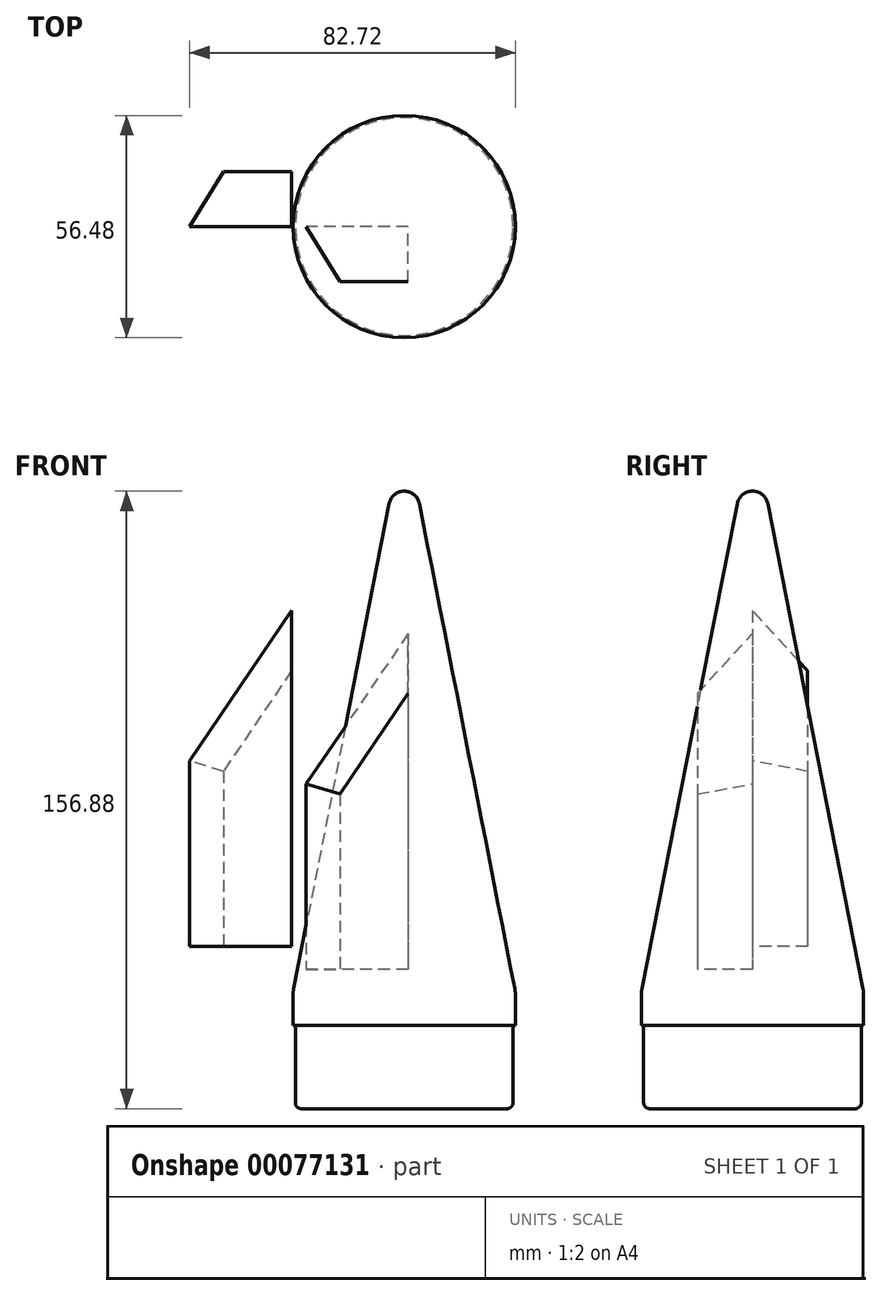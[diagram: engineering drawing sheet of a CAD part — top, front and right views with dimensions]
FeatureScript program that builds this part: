
annotation { "Feature Type Name" : "Feature", "Feature Type Description" : "" }
export const myFeature = defineFeature(function(context is Context, id is Id, definition is map)
    precondition{}
    {
        {
            var Q0;
            Q0=qCreatedBy(makeId("Front.planeOp"),FACE);
            var sketch = newSketch(context, id + "F0", { "sketchPlane" : qUnion([Q0])});
            skLineSegment(sketch, "E0", {"start": v(-33.3, -70.07) * mm, "end": v(-33.3, -70.07) * mm});
            skLineSegment(sketch, "E1", {"start": v(0, -70.07) * mm, "end": v(0, 79.93) * mm});
            skLineSegment(sketch, "E2", {"start": v(0, -70.07) * mm, "end": v(0, -80.07) * mm});
            skLineSegment(sketch, "E3", {"start": v(-32.6, -80.07) * mm, "end": v(-33.3, -80.07) * mm});
            skLineSegment(sketch, "E4", {"start": v(-33.3, -80.07) * mm, "end": v(-33.3, -70.07) * mm});
            skPoint(sketch, "E5.orphan", {"position": v(0, 86.63) * mm});
            skLineSegment(sketch, "E6", {"start": v(-33.3, -70.07) * mm, "end": v(-4.56, 76.18) * mm});
            skLineSegment(sketch, "E7.top", {"start": v(0, -105.07) * mm, "end": v(-32.6, -105.07) * mm});
            skLineSegment(sketch, "E7.left", {"start": v(0, -80.07) * mm, "end": v(0, -105.07) * mm});
            skLineSegment(sketch, "E7.right", {"start": v(-32.6, -80.07) * mm, "end": v(-32.6, -105.07) * mm});
            skArc(sketch, "E8", {"start": v(0, 79.93) * mm, "mid": v(-2.95, 78.87) * mm, "end": v(-4.56, 76.18) * mm});
            skSolve(sketch);
        }
        {
            var Q0;
            {var subQ0=sQuery(id+"F0.wireOp",EDGE,"E2");Q0=makeQuery(id+"F0.imprint","IMPRINT",FACE,{"disambiguationData":[TD([[makeQuery(id+"F0.imprint","IMPRINT",EDGE,{"derivedFrom":subQ0}),-1.0]])]});}
            var Q1;
            Q1=sQuery(id+"F0.wireOp",EDGE,"E1");
            revolve(context, id + "F1", {"entities" : qUnion([Q0]), "axis" : qUnion([Q1]), "revolveType" : RevolveType.FULL});
        }
        {
            var Q0;
            Q0=makeQuery(id+"F1.opRevolve","SWEPT_BODY",BODY,{"disambiguationData":[OSD([sQuery(id+"F0.wireOp",EDGE,"Oh61cgLR-RQo2-T4aV-TcRg-Gp7ijPdUG9jl"),sQuery(id+"F0.wireOp",EDGE,"E1"),sQuery(id+"F0.wireOp",EDGE,"E2"),sQuery(id+"F0.wireOp",EDGE,"E3"),sQuery(id+"F0.wireOp",EDGE,"E4"),sQuery(id+"F0.wireOp",EDGE,"E0"),sQuery(id+"F0.wireOp",EDGE,"dTV1AxgJ-VMAe-DLQO-Zqz3-4UbtDb8FiUJC")])]});
            var Q1;
            Q1=qCreatedBy(makeId("Origin.pointOp"),VERTEX);
            transform(context, id + "F2", {"entities" : qUnion([Q0]), "transformType" : TransformType.SCALE_UNIFORMLY, "scale" : .848, "scalePoint" : qUnion([Q1]), "makeCopy" : false});
        }
        {
            var Q0;
            Q0=qCreatedBy(makeId("Front.planeOp"),FACE);
            var sketch = newSketch(context, id + "F3", { "sketchPlane" : qUnion([Q0])});
            skLineSegment(sketch, "E9", {"start": v(-56.93, -47.9) * mm, "end": v(-56.93, 0) * mm});
            skLineSegment(sketch, "E10", {"start": v(-56.93, 0) * mm, "end": v(-28.6, 41.78) * mm});
            skLineSegment(sketch, "E11", {"start": v(-28.6, 41.78) * mm, "end": v(-28.6, -47.9) * mm});
            skLineSegment(sketch, "E12", {"start": v(-28.6, -47.9) * mm, "end": v(-56.93, -47.9) * mm});
            skSolve(sketch);
        }
        {
            var Q0;
            Q0=makeQuery(id+"F3.imprint","IMPRINT",FACE,{"disambiguationData":[TD([[makeQuery(id+"F3.imprint","IMPRINT",EDGE,{"derivedFrom":sQuery(id+"F3.wireOp",EDGE,"E9")}),-1.0]])]});
            extrude(context, id + "F4", {"entities" : qUnion([Q0]), "depth" : 14 * mm, "offsetDistance" : 25 * mm});
        }
        {
            var Q0;
            Q0=makeQuery(id+"F4.opExtrude","CAP_EDGE",EDGE,{"disambiguationData":[OSD([sQuery(id+"F3.wireOp",EDGE,"E10")])],"isStart":false});
            var Q1;
            Q1=makeQuery(id+"F4.opExtrude","CAP_EDGE",EDGE,{"disambiguationData":[OSD([sQuery(id+"F3.wireOp",EDGE,"E9")])],"isStart":false});
            chamfer(context, id + "F5", {"entities" : qUnion([Q0, Q1]), "chamferType" : ChamferType.TWO_OFFSETS, "width1" : 11 * mm, "oppositeDirection" : false, "width2" : 18 * mm, "tangentPropagation" : true});
        }
        {
            var Q0;
            Q0=makeQuery(id+"F4.opExtrude","SWEPT_BODY",BODY,{"disambiguationData":[OSD([sQuery(id+"F3.wireOp",EDGE,"E9"),sQuery(id+"F3.wireOp",EDGE,"E10"),sQuery(id+"F3.wireOp",EDGE,"E11"),sQuery(id+"F3.wireOp",EDGE,"E12")])]});
            var Q1;
            Q1=qCreatedBy(makeId("Front.planeOp"),FACE);
            mirror(context, id + "F6", {"operationType" : NewBodyOperationType.ADD, "entities" : qUnion([Q0]), "mirrorPlane" : qUnion([Q1])});
        }
        {
            var Q0;
            Q0=makeQuery(id+"F4.opExtrude","SWEPT_BODY",BODY,{"disambiguationData":[OSD([sQuery(id+"F3.wireOp",EDGE,"E9"),sQuery(id+"F3.wireOp",EDGE,"E10"),sQuery(id+"F3.wireOp",EDGE,"E11"),sQuery(id+"F3.wireOp",EDGE,"E12")])]});
            transform(context, id + "F7", {"entities" : qUnion([Q0]), "transformType" : TransformType.TRANSLATION_3D, "dx" : 29.6 * mm, "dy" : 0 * mm, "dz" : -5.8 * mm, "makeCopy" : false});
        }
        {
            var Q0;
            Q0=makeQuery(id+"F1.opRevolve","SWEPT_EDGE",EDGE,{"disambiguationData":[OSD([sQuery(id+"F0.wireOp",EDGE,"E4"),sQuery(id+"F0.wireOp",EDGE,"E6")])]});
            fillet(context, id + "F8", {"entities" : qUnion([Q0]), "radius" : 7.8 * mm, "tangentPropagation" : true, "allowEdgeOverflow" : false});
        }
        {
            var Q0;
            Q0=makeQuery(id+"F1.opRevolve","SWEPT_EDGE",EDGE,{"disambiguationData":[OSD([sQuery(id+"F0.wireOp",EDGE,"E7.top"),sQuery(id+"F0.wireOp",EDGE,"E7.right")])]});
            fillet(context, id + "F9", {"entities" : qUnion([Q0]), "radius" : 1.5 * mm, "tangentPropagation" : true, "allowEdgeOverflow" : false});
        }
        {
            var Q0;
            Q0=qCreatedBy(makeId("Top.planeOp"),FACE);
            cPlane(context, id + "F10", {"entities" : qUnion([Q0]), "cplaneType" : CPlaneType.OFFSET, "offset" : 25 * mm, "oppositeDirection" : true, "width" : 150 * mm, "height" : 150 * mm});
        }
        {
            var Q0;
            Q0=qCreatedBy(makeId("Front.planeOp"),FACE);
            cPlane(context, id + "F12", {"entities" : qUnion([Q0]), "cplaneType" : CPlaneType.OFFSET, "offset" : 35 * mm, "width" : 150 * mm, "height" : 150 * mm});
        }
        {
            var Q0;
            Q0=qCreatedBy(id+"F12.planeOp",FACE);
            var sketch = newSketch(context, id + "F13", { "sketchPlane" : qUnion([Q0])});
            skText(sketch, "E13", { "text": "DC3Dparts", "fontName": "OpenSans-Regular.ttf"});
            const initialGuessF13  = {"E13": [-0.024, -0.07859, 1, 0, 0.007]};
            skSetInitialGuess(sketch, initialGuessF13);
            skSolve(sketch);
        }
        {
            var Q0;
            Q0=qSketchRegion(id+"F13",true);
            var Q1;
            Q1=qCreatedBy(makeId("Front.planeOp"),FACE);
            extrude(context, id + "F14", {"entities" : qUnion([Q0]), "endBound" : BoundingType.UP_TO_SURFACE, "oppositeDirection" : true, "depth" : 25 * mm, "endBoundEntityFace" : qUnion([Q1]), "offsetDistance" : 25 * mm});
        }
        {
            var Q0;
            Q0=qCreatedBy(makeId("Front.planeOp"),FACE);
            var sketch = newSketch(context, id + "F15", { "sketchPlane" : qUnion([Q0])});
            skLineSegment(sketch, "E14.bottom", {"start": v(0, -64.71) * mm, "end": v(-27, -64.71) * mm});
            skLineSegment(sketch, "E14.top", {"start": v(0, -103.72) * mm, "end": v(-27, -103.72) * mm});
            skLineSegment(sketch, "E14.left", {"start": v(0, -64.71) * mm, "end": v(0, -103.72) * mm});
            skLineSegment(sketch, "E14.right", {"start": v(-27, -64.71) * mm, "end": v(-27, -103.72) * mm});
            skSolve(sketch);
        }
        {
            var Q0;
            Q0=makeQuery(id+"F15.imprint","IMPRINT",FACE,{"disambiguationData":[TD([[makeQuery(id+"F15.imprint","IMPRINT",EDGE,{"derivedFrom":sQuery(id+"F15.wireOp",EDGE,"E14.bottom")}),1.0]])]});
            var Q1;
            Q1=sQuery(id+"F15.wireOp",EDGE,"E14.left");
            revolve(context, id + "F16", {"entities" : qUnion([Q0]), "axis" : qUnion([Q1]), "revolveType" : RevolveType.FULL});
        }
        {
            var Q0;
            Q0=makeQuery(id+"F16.opRevolve","SWEPT_BODY",BODY,{"disambiguationData":[OSD([sQuery(id+"F15.wireOp",EDGE,"E14.bottom"),sQuery(id+"F15.wireOp",EDGE,"E14.top"),sQuery(id+"F15.wireOp",EDGE,"E14.left"),sQuery(id+"F15.wireOp",EDGE,"E14.right")])]});
            var Q1;
            Q1=makeQuery(id+"F14.opExtrude","SWEPT_BODY",BODY,{"disambiguationData":[OSD([sQuery(id+"F13.wireOp",EDGE,"E13.sketch_text.stroke-0"),sQuery(id+"F13.wireOp",EDGE,"E13.sketch_text.stroke-1"),sQuery(id+"F13.wireOp",EDGE,"E13.sketch_text.stroke-2"),sQuery(id+"F13.wireOp",EDGE,"E13.sketch_text.stroke-3"),sQuery(id+"F13.wireOp",EDGE,"E13.sketch_text.stroke-4"),sQuery(id+"F13.wireOp",EDGE,"E13.sketch_text.stroke-5"),sQuery(id+"F13.wireOp",EDGE,"E13.sketch_text.stroke-6"),sQuery(id+"F13.wireOp",EDGE,"E13.sketch_text.stroke-7"),sQuery(id+"F13.wireOp",EDGE,"E13.sketch_text.stroke-8"),sQuery(id+"F13.wireOp",EDGE,"E13.sketch_text.stroke-9"),sQuery(id+"F13.wireOp",EDGE,"E13.sketch_text.stroke-10"),sQuery(id+"F13.wireOp",EDGE,"E13.sketch_text.stroke-11"),sQuery(id+"F13.wireOp",EDGE,"E13.sketch_text.stroke-12"),sQuery(id+"F13.wireOp",EDGE,"E13.sketch_text.stroke-13")])]});
            var Q2;
            Q2=makeQuery(id+"F14.opExtrude","SWEPT_BODY",BODY,{"disambiguationData":[OSD([sQuery(id+"F13.wireOp",EDGE,"E13.sketch_text.stroke-14"),sQuery(id+"F13.wireOp",EDGE,"E13.sketch_text.stroke-15"),sQuery(id+"F13.wireOp",EDGE,"E13.sketch_text.stroke-16"),sQuery(id+"F13.wireOp",EDGE,"E13.sketch_text.stroke-17"),sQuery(id+"F13.wireOp",EDGE,"E13.sketch_text.stroke-18"),sQuery(id+"F13.wireOp",EDGE,"E13.sketch_text.stroke-19"),sQuery(id+"F13.wireOp",EDGE,"E13.sketch_text.stroke-20"),sQuery(id+"F13.wireOp",EDGE,"E13.sketch_text.stroke-21"),sQuery(id+"F13.wireOp",EDGE,"E13.sketch_text.stroke-22"),sQuery(id+"F13.wireOp",EDGE,"E13.sketch_text.stroke-23"),sQuery(id+"F13.wireOp",EDGE,"E13.sketch_text.stroke-24"),sQuery(id+"F13.wireOp",EDGE,"E13.sketch_text.stroke-25"),sQuery(id+"F13.wireOp",EDGE,"E13.sketch_text.stroke-26"),sQuery(id+"F13.wireOp",EDGE,"E13.sketch_text.stroke-27"),sQuery(id+"F13.wireOp",EDGE,"E13.sketch_text.stroke-28")])]});
            var Q3;
            Q3=makeQuery(id+"F14.opExtrude","SWEPT_BODY",BODY,{"disambiguationData":[OSD([sQuery(id+"F13.wireOp",EDGE,"E13.sketch_text.stroke-29"),sQuery(id+"F13.wireOp",EDGE,"E13.sketch_text.stroke-30"),sQuery(id+"F13.wireOp",EDGE,"E13.sketch_text.stroke-31"),sQuery(id+"F13.wireOp",EDGE,"E13.sketch_text.stroke-32"),sQuery(id+"F13.wireOp",EDGE,"E13.sketch_text.stroke-33"),sQuery(id+"F13.wireOp",EDGE,"E13.sketch_text.stroke-34"),sQuery(id+"F13.wireOp",EDGE,"E13.sketch_text.stroke-35"),sQuery(id+"F13.wireOp",EDGE,"E13.sketch_text.stroke-36"),sQuery(id+"F13.wireOp",EDGE,"E13.sketch_text.stroke-37"),sQuery(id+"F13.wireOp",EDGE,"E13.sketch_text.stroke-38"),sQuery(id+"F13.wireOp",EDGE,"E13.sketch_text.stroke-39"),sQuery(id+"F13.wireOp",EDGE,"E13.sketch_text.stroke-40"),sQuery(id+"F13.wireOp",EDGE,"E13.sketch_text.stroke-41"),sQuery(id+"F13.wireOp",EDGE,"E13.sketch_text.stroke-42"),sQuery(id+"F13.wireOp",EDGE,"E13.sketch_text.stroke-43"),sQuery(id+"F13.wireOp",EDGE,"E13.sketch_text.stroke-44"),sQuery(id+"F13.wireOp",EDGE,"E13.sketch_text.stroke-45"),sQuery(id+"F13.wireOp",EDGE,"E13.sketch_text.stroke-46"),sQuery(id+"F13.wireOp",EDGE,"E13.sketch_text.stroke-47"),sQuery(id+"F13.wireOp",EDGE,"E13.sketch_text.stroke-48"),sQuery(id+"F13.wireOp",EDGE,"E13.sketch_text.stroke-49"),sQuery(id+"F13.wireOp",EDGE,"E13.sketch_text.stroke-50"),sQuery(id+"F13.wireOp",EDGE,"E13.sketch_text.stroke-51"),sQuery(id+"F13.wireOp",EDGE,"E13.sketch_text.stroke-52"),sQuery(id+"F13.wireOp",EDGE,"E13.sketch_text.stroke-53"),sQuery(id+"F13.wireOp",EDGE,"E13.sketch_text.stroke-54"),sQuery(id+"F13.wireOp",EDGE,"E13.sketch_text.stroke-55"),sQuery(id+"F13.wireOp",EDGE,"E13.sketch_text.stroke-56")])]});
            var Q4;
            Q4=makeQuery(id+"F14.opExtrude","SWEPT_BODY",BODY,{"disambiguationData":[OSD([sQuery(id+"F13.wireOp",EDGE,"E13.sketch_text.stroke-57"),sQuery(id+"F13.wireOp",EDGE,"E13.sketch_text.stroke-58"),sQuery(id+"F13.wireOp",EDGE,"E13.sketch_text.stroke-59"),sQuery(id+"F13.wireOp",EDGE,"E13.sketch_text.stroke-60"),sQuery(id+"F13.wireOp",EDGE,"E13.sketch_text.stroke-61"),sQuery(id+"F13.wireOp",EDGE,"E13.sketch_text.stroke-62"),sQuery(id+"F13.wireOp",EDGE,"E13.sketch_text.stroke-63"),sQuery(id+"F13.wireOp",EDGE,"E13.sketch_text.stroke-64"),sQuery(id+"F13.wireOp",EDGE,"E13.sketch_text.stroke-65"),sQuery(id+"F13.wireOp",EDGE,"E13.sketch_text.stroke-66"),sQuery(id+"F13.wireOp",EDGE,"E13.sketch_text.stroke-67"),sQuery(id+"F13.wireOp",EDGE,"E13.sketch_text.stroke-68"),sQuery(id+"F13.wireOp",EDGE,"E13.sketch_text.stroke-69"),sQuery(id+"F13.wireOp",EDGE,"E13.sketch_text.stroke-70")])]});
            var Q5;
            Q5=makeQuery(id+"F14.opExtrude","SWEPT_BODY",BODY,{"disambiguationData":[OSD([sQuery(id+"F13.wireOp",EDGE,"E13.sketch_text.stroke-71"),sQuery(id+"F13.wireOp",EDGE,"E13.sketch_text.stroke-72"),sQuery(id+"F13.wireOp",EDGE,"E13.sketch_text.stroke-73"),sQuery(id+"F13.wireOp",EDGE,"E13.sketch_text.stroke-74"),sQuery(id+"F13.wireOp",EDGE,"E13.sketch_text.stroke-75"),sQuery(id+"F13.wireOp",EDGE,"E13.sketch_text.stroke-76"),sQuery(id+"F13.wireOp",EDGE,"E13.sketch_text.stroke-77"),sQuery(id+"F13.wireOp",EDGE,"E13.sketch_text.stroke-78"),sQuery(id+"F13.wireOp",EDGE,"E13.sketch_text.stroke-79"),sQuery(id+"F13.wireOp",EDGE,"E13.sketch_text.stroke-80"),sQuery(id+"F13.wireOp",EDGE,"E13.sketch_text.stroke-81"),sQuery(id+"F13.wireOp",EDGE,"E13.sketch_text.stroke-82"),sQuery(id+"F13.wireOp",EDGE,"E13.sketch_text.stroke-83"),sQuery(id+"F13.wireOp",EDGE,"E13.sketch_text.stroke-84"),sQuery(id+"F13.wireOp",EDGE,"E13.sketch_text.stroke-85"),sQuery(id+"F13.wireOp",EDGE,"E13.sketch_text.stroke-86"),sQuery(id+"F13.wireOp",EDGE,"E13.sketch_text.stroke-87"),sQuery(id+"F13.wireOp",EDGE,"E13.sketch_text.stroke-88"),sQuery(id+"F13.wireOp",EDGE,"E13.sketch_text.stroke-89"),sQuery(id+"F13.wireOp",EDGE,"E13.sketch_text.stroke-90"),sQuery(id+"F13.wireOp",EDGE,"E13.sketch_text.stroke-91"),sQuery(id+"F13.wireOp",EDGE,"E13.sketch_text.stroke-92"),sQuery(id+"F13.wireOp",EDGE,"E13.sketch_text.stroke-93"),sQuery(id+"F13.wireOp",EDGE,"E13.sketch_text.stroke-94"),sQuery(id+"F13.wireOp",EDGE,"E13.sketch_text.stroke-95")])]});
            var Q6;
            Q6=makeQuery(id+"F14.opExtrude","SWEPT_BODY",BODY,{"disambiguationData":[OSD([sQuery(id+"F13.wireOp",EDGE,"E13.sketch_text.stroke-96"),sQuery(id+"F13.wireOp",EDGE,"E13.sketch_text.stroke-97"),sQuery(id+"F13.wireOp",EDGE,"E13.sketch_text.stroke-98"),sQuery(id+"F13.wireOp",EDGE,"E13.sketch_text.stroke-99"),sQuery(id+"F13.wireOp",EDGE,"E13.sketch_text.stroke-100"),sQuery(id+"F13.wireOp",EDGE,"E13.sketch_text.stroke-101"),sQuery(id+"F13.wireOp",EDGE,"E13.sketch_text.stroke-102"),sQuery(id+"F13.wireOp",EDGE,"E13.sketch_text.stroke-103"),sQuery(id+"F13.wireOp",EDGE,"E13.sketch_text.stroke-104"),sQuery(id+"F13.wireOp",EDGE,"E13.sketch_text.stroke-105"),sQuery(id+"F13.wireOp",EDGE,"E13.sketch_text.stroke-106"),sQuery(id+"F13.wireOp",EDGE,"E13.sketch_text.stroke-107"),sQuery(id+"F13.wireOp",EDGE,"E13.sketch_text.stroke-108"),sQuery(id+"F13.wireOp",EDGE,"E13.sketch_text.stroke-109"),sQuery(id+"F13.wireOp",EDGE,"E13.sketch_text.stroke-110"),sQuery(id+"F13.wireOp",EDGE,"E13.sketch_text.stroke-111"),sQuery(id+"F13.wireOp",EDGE,"E13.sketch_text.stroke-112"),sQuery(id+"F13.wireOp",EDGE,"E13.sketch_text.stroke-113"),sQuery(id+"F13.wireOp",EDGE,"E13.sketch_text.stroke-114"),sQuery(id+"F13.wireOp",EDGE,"E13.sketch_text.stroke-115"),sQuery(id+"F13.wireOp",EDGE,"E13.sketch_text.stroke-116"),sQuery(id+"F13.wireOp",EDGE,"E13.sketch_text.stroke-117"),sQuery(id+"F13.wireOp",EDGE,"E13.sketch_text.stroke-118"),sQuery(id+"F13.wireOp",EDGE,"E13.sketch_text.stroke-119"),sQuery(id+"F13.wireOp",EDGE,"E13.sketch_text.stroke-120"),sQuery(id+"F13.wireOp",EDGE,"E13.sketch_text.stroke-121"),sQuery(id+"F13.wireOp",EDGE,"E13.sketch_text.stroke-122")])]});
            var Q7;
            Q7=makeQuery(id+"F14.opExtrude","SWEPT_BODY",BODY,{"disambiguationData":[OSD([sQuery(id+"F13.wireOp",EDGE,"E13.sketch_text.stroke-123"),sQuery(id+"F13.wireOp",EDGE,"E13.sketch_text.stroke-124"),sQuery(id+"F13.wireOp",EDGE,"E13.sketch_text.stroke-125"),sQuery(id+"F13.wireOp",EDGE,"E13.sketch_text.stroke-126"),sQuery(id+"F13.wireOp",EDGE,"E13.sketch_text.stroke-127"),sQuery(id+"F13.wireOp",EDGE,"E13.sketch_text.stroke-128"),sQuery(id+"F13.wireOp",EDGE,"E13.sketch_text.stroke-129"),sQuery(id+"F13.wireOp",EDGE,"E13.sketch_text.stroke-130"),sQuery(id+"F13.wireOp",EDGE,"E13.sketch_text.stroke-131"),sQuery(id+"F13.wireOp",EDGE,"E13.sketch_text.stroke-132"),sQuery(id+"F13.wireOp",EDGE,"E13.sketch_text.stroke-133"),sQuery(id+"F13.wireOp",EDGE,"E13.sketch_text.stroke-134"),sQuery(id+"F13.wireOp",EDGE,"E13.sketch_text.stroke-135")])]});
            var Q8;
            Q8=makeQuery(id+"F14.opExtrude","SWEPT_BODY",BODY,{"disambiguationData":[OSD([sQuery(id+"F13.wireOp",EDGE,"E13.sketch_text.stroke-136"),sQuery(id+"F13.wireOp",EDGE,"E13.sketch_text.stroke-137"),sQuery(id+"F13.wireOp",EDGE,"E13.sketch_text.stroke-138"),sQuery(id+"F13.wireOp",EDGE,"E13.sketch_text.stroke-139"),sQuery(id+"F13.wireOp",EDGE,"E13.sketch_text.stroke-140"),sQuery(id+"F13.wireOp",EDGE,"E13.sketch_text.stroke-141"),sQuery(id+"F13.wireOp",EDGE,"E13.sketch_text.stroke-142"),sQuery(id+"F13.wireOp",EDGE,"E13.sketch_text.stroke-143"),sQuery(id+"F13.wireOp",EDGE,"E13.sketch_text.stroke-144"),sQuery(id+"F13.wireOp",EDGE,"E13.sketch_text.stroke-145"),sQuery(id+"F13.wireOp",EDGE,"E13.sketch_text.stroke-146"),sQuery(id+"F13.wireOp",EDGE,"E13.sketch_text.stroke-147"),sQuery(id+"F13.wireOp",EDGE,"E13.sketch_text.stroke-148"),sQuery(id+"F13.wireOp",EDGE,"E13.sketch_text.stroke-149"),sQuery(id+"F13.wireOp",EDGE,"E13.sketch_text.stroke-150"),sQuery(id+"F13.wireOp",EDGE,"E13.sketch_text.stroke-151"),sQuery(id+"F13.wireOp",EDGE,"E13.sketch_text.stroke-152"),sQuery(id+"F13.wireOp",EDGE,"E13.sketch_text.stroke-153"),sQuery(id+"F13.wireOp",EDGE,"E13.sketch_text.stroke-154")])]});
            var Q9;
            Q9=makeQuery(id+"F14.opExtrude","SWEPT_BODY",BODY,{"disambiguationData":[OSD([sQuery(id+"F13.wireOp",EDGE,"E13.sketch_text.stroke-155"),sQuery(id+"F13.wireOp",EDGE,"E13.sketch_text.stroke-156"),sQuery(id+"F13.wireOp",EDGE,"E13.sketch_text.stroke-157"),sQuery(id+"F13.wireOp",EDGE,"E13.sketch_text.stroke-158"),sQuery(id+"F13.wireOp",EDGE,"E13.sketch_text.stroke-159"),sQuery(id+"F13.wireOp",EDGE,"E13.sketch_text.stroke-160"),sQuery(id+"F13.wireOp",EDGE,"E13.sketch_text.stroke-161"),sQuery(id+"F13.wireOp",EDGE,"E13.sketch_text.stroke-162"),sQuery(id+"F13.wireOp",EDGE,"E13.sketch_text.stroke-163"),sQuery(id+"F13.wireOp",EDGE,"E13.sketch_text.stroke-164"),sQuery(id+"F13.wireOp",EDGE,"E13.sketch_text.stroke-165"),sQuery(id+"F13.wireOp",EDGE,"E13.sketch_text.stroke-166"),sQuery(id+"F13.wireOp",EDGE,"E13.sketch_text.stroke-167"),sQuery(id+"F13.wireOp",EDGE,"E13.sketch_text.stroke-168"),sQuery(id+"F13.wireOp",EDGE,"E13.sketch_text.stroke-169"),sQuery(id+"F13.wireOp",EDGE,"E13.sketch_text.stroke-170"),sQuery(id+"F13.wireOp",EDGE,"E13.sketch_text.stroke-171"),sQuery(id+"F13.wireOp",EDGE,"E13.sketch_text.stroke-172"),sQuery(id+"F13.wireOp",EDGE,"E13.sketch_text.stroke-173"),sQuery(id+"F13.wireOp",EDGE,"E13.sketch_text.stroke-174"),sQuery(id+"F13.wireOp",EDGE,"E13.sketch_text.stroke-175"),sQuery(id+"F13.wireOp",EDGE,"E13.sketch_text.stroke-176"),sQuery(id+"F13.wireOp",EDGE,"E13.sketch_text.stroke-177"),sQuery(id+"F13.wireOp",EDGE,"E13.sketch_text.stroke-178"),sQuery(id+"F13.wireOp",EDGE,"E13.sketch_text.stroke-179")])]});
            booleanBodies(context, id + "F17", {"operationType" : BooleanOperationType.SUBTRACTION, "tools" : qUnion([Q0]), "targets" : qUnion([Q1, Q2, Q3, Q4, Q5, Q6, Q7, Q8, Q9])});
        }
        {
            var Q0;
            Q0=makeQuery(id+"F14.opExtrude","SWEPT_BODY",BODY,{"disambiguationData":[OSD([sQuery(id+"F13.wireOp",EDGE,"E13.sketch_text.stroke-0"),sQuery(id+"F13.wireOp",EDGE,"E13.sketch_text.stroke-1"),sQuery(id+"F13.wireOp",EDGE,"E13.sketch_text.stroke-2"),sQuery(id+"F13.wireOp",EDGE,"E13.sketch_text.stroke-3"),sQuery(id+"F13.wireOp",EDGE,"E13.sketch_text.stroke-4"),sQuery(id+"F13.wireOp",EDGE,"E13.sketch_text.stroke-5"),sQuery(id+"F13.wireOp",EDGE,"E13.sketch_text.stroke-6"),sQuery(id+"F13.wireOp",EDGE,"E13.sketch_text.stroke-7"),sQuery(id+"F13.wireOp",EDGE,"E13.sketch_text.stroke-8"),sQuery(id+"F13.wireOp",EDGE,"E13.sketch_text.stroke-9"),sQuery(id+"F13.wireOp",EDGE,"E13.sketch_text.stroke-10"),sQuery(id+"F13.wireOp",EDGE,"E13.sketch_text.stroke-11"),sQuery(id+"F13.wireOp",EDGE,"E13.sketch_text.stroke-12"),sQuery(id+"F13.wireOp",EDGE,"E13.sketch_text.stroke-13")])]});
            var Q1;
            Q1=makeQuery(id+"F14.opExtrude","SWEPT_BODY",BODY,{"disambiguationData":[OSD([sQuery(id+"F13.wireOp",EDGE,"E13.sketch_text.stroke-14"),sQuery(id+"F13.wireOp",EDGE,"E13.sketch_text.stroke-15"),sQuery(id+"F13.wireOp",EDGE,"E13.sketch_text.stroke-16"),sQuery(id+"F13.wireOp",EDGE,"E13.sketch_text.stroke-17"),sQuery(id+"F13.wireOp",EDGE,"E13.sketch_text.stroke-18"),sQuery(id+"F13.wireOp",EDGE,"E13.sketch_text.stroke-19"),sQuery(id+"F13.wireOp",EDGE,"E13.sketch_text.stroke-20"),sQuery(id+"F13.wireOp",EDGE,"E13.sketch_text.stroke-21"),sQuery(id+"F13.wireOp",EDGE,"E13.sketch_text.stroke-22"),sQuery(id+"F13.wireOp",EDGE,"E13.sketch_text.stroke-23"),sQuery(id+"F13.wireOp",EDGE,"E13.sketch_text.stroke-24"),sQuery(id+"F13.wireOp",EDGE,"E13.sketch_text.stroke-25"),sQuery(id+"F13.wireOp",EDGE,"E13.sketch_text.stroke-26"),sQuery(id+"F13.wireOp",EDGE,"E13.sketch_text.stroke-27"),sQuery(id+"F13.wireOp",EDGE,"E13.sketch_text.stroke-28")])]});
            var Q2;
            Q2=makeQuery(id+"F14.opExtrude","SWEPT_BODY",BODY,{"disambiguationData":[OSD([sQuery(id+"F13.wireOp",EDGE,"E13.sketch_text.stroke-29"),sQuery(id+"F13.wireOp",EDGE,"E13.sketch_text.stroke-30"),sQuery(id+"F13.wireOp",EDGE,"E13.sketch_text.stroke-31"),sQuery(id+"F13.wireOp",EDGE,"E13.sketch_text.stroke-32"),sQuery(id+"F13.wireOp",EDGE,"E13.sketch_text.stroke-33"),sQuery(id+"F13.wireOp",EDGE,"E13.sketch_text.stroke-34"),sQuery(id+"F13.wireOp",EDGE,"E13.sketch_text.stroke-35"),sQuery(id+"F13.wireOp",EDGE,"E13.sketch_text.stroke-36"),sQuery(id+"F13.wireOp",EDGE,"E13.sketch_text.stroke-37"),sQuery(id+"F13.wireOp",EDGE,"E13.sketch_text.stroke-38"),sQuery(id+"F13.wireOp",EDGE,"E13.sketch_text.stroke-39"),sQuery(id+"F13.wireOp",EDGE,"E13.sketch_text.stroke-40"),sQuery(id+"F13.wireOp",EDGE,"E13.sketch_text.stroke-41"),sQuery(id+"F13.wireOp",EDGE,"E13.sketch_text.stroke-42"),sQuery(id+"F13.wireOp",EDGE,"E13.sketch_text.stroke-43"),sQuery(id+"F13.wireOp",EDGE,"E13.sketch_text.stroke-44"),sQuery(id+"F13.wireOp",EDGE,"E13.sketch_text.stroke-45"),sQuery(id+"F13.wireOp",EDGE,"E13.sketch_text.stroke-46"),sQuery(id+"F13.wireOp",EDGE,"E13.sketch_text.stroke-47"),sQuery(id+"F13.wireOp",EDGE,"E13.sketch_text.stroke-48"),sQuery(id+"F13.wireOp",EDGE,"E13.sketch_text.stroke-49"),sQuery(id+"F13.wireOp",EDGE,"E13.sketch_text.stroke-50"),sQuery(id+"F13.wireOp",EDGE,"E13.sketch_text.stroke-51"),sQuery(id+"F13.wireOp",EDGE,"E13.sketch_text.stroke-52"),sQuery(id+"F13.wireOp",EDGE,"E13.sketch_text.stroke-53"),sQuery(id+"F13.wireOp",EDGE,"E13.sketch_text.stroke-54"),sQuery(id+"F13.wireOp",EDGE,"E13.sketch_text.stroke-55"),sQuery(id+"F13.wireOp",EDGE,"E13.sketch_text.stroke-56")])]});
            var Q3;
            Q3=makeQuery(id+"F14.opExtrude","SWEPT_BODY",BODY,{"disambiguationData":[OSD([sQuery(id+"F13.wireOp",EDGE,"E13.sketch_text.stroke-57"),sQuery(id+"F13.wireOp",EDGE,"E13.sketch_text.stroke-58"),sQuery(id+"F13.wireOp",EDGE,"E13.sketch_text.stroke-59"),sQuery(id+"F13.wireOp",EDGE,"E13.sketch_text.stroke-60"),sQuery(id+"F13.wireOp",EDGE,"E13.sketch_text.stroke-61"),sQuery(id+"F13.wireOp",EDGE,"E13.sketch_text.stroke-62"),sQuery(id+"F13.wireOp",EDGE,"E13.sketch_text.stroke-63"),sQuery(id+"F13.wireOp",EDGE,"E13.sketch_text.stroke-64"),sQuery(id+"F13.wireOp",EDGE,"E13.sketch_text.stroke-65"),sQuery(id+"F13.wireOp",EDGE,"E13.sketch_text.stroke-66"),sQuery(id+"F13.wireOp",EDGE,"E13.sketch_text.stroke-67"),sQuery(id+"F13.wireOp",EDGE,"E13.sketch_text.stroke-68"),sQuery(id+"F13.wireOp",EDGE,"E13.sketch_text.stroke-69"),sQuery(id+"F13.wireOp",EDGE,"E13.sketch_text.stroke-70")])]});
            var Q4;
            Q4=makeQuery(id+"F14.opExtrude","SWEPT_BODY",BODY,{"disambiguationData":[OSD([sQuery(id+"F13.wireOp",EDGE,"E13.sketch_text.stroke-71"),sQuery(id+"F13.wireOp",EDGE,"E13.sketch_text.stroke-72"),sQuery(id+"F13.wireOp",EDGE,"E13.sketch_text.stroke-73"),sQuery(id+"F13.wireOp",EDGE,"E13.sketch_text.stroke-74"),sQuery(id+"F13.wireOp",EDGE,"E13.sketch_text.stroke-75"),sQuery(id+"F13.wireOp",EDGE,"E13.sketch_text.stroke-76"),sQuery(id+"F13.wireOp",EDGE,"E13.sketch_text.stroke-77"),sQuery(id+"F13.wireOp",EDGE,"E13.sketch_text.stroke-78"),sQuery(id+"F13.wireOp",EDGE,"E13.sketch_text.stroke-79"),sQuery(id+"F13.wireOp",EDGE,"E13.sketch_text.stroke-80"),sQuery(id+"F13.wireOp",EDGE,"E13.sketch_text.stroke-81"),sQuery(id+"F13.wireOp",EDGE,"E13.sketch_text.stroke-82"),sQuery(id+"F13.wireOp",EDGE,"E13.sketch_text.stroke-83"),sQuery(id+"F13.wireOp",EDGE,"E13.sketch_text.stroke-84"),sQuery(id+"F13.wireOp",EDGE,"E13.sketch_text.stroke-85"),sQuery(id+"F13.wireOp",EDGE,"E13.sketch_text.stroke-86"),sQuery(id+"F13.wireOp",EDGE,"E13.sketch_text.stroke-87"),sQuery(id+"F13.wireOp",EDGE,"E13.sketch_text.stroke-88"),sQuery(id+"F13.wireOp",EDGE,"E13.sketch_text.stroke-89"),sQuery(id+"F13.wireOp",EDGE,"E13.sketch_text.stroke-90"),sQuery(id+"F13.wireOp",EDGE,"E13.sketch_text.stroke-91"),sQuery(id+"F13.wireOp",EDGE,"E13.sketch_text.stroke-92"),sQuery(id+"F13.wireOp",EDGE,"E13.sketch_text.stroke-93"),sQuery(id+"F13.wireOp",EDGE,"E13.sketch_text.stroke-94"),sQuery(id+"F13.wireOp",EDGE,"E13.sketch_text.stroke-95")])]});
            var Q5;
            Q5=makeQuery(id+"F14.opExtrude","SWEPT_BODY",BODY,{"disambiguationData":[OSD([sQuery(id+"F13.wireOp",EDGE,"E13.sketch_text.stroke-96"),sQuery(id+"F13.wireOp",EDGE,"E13.sketch_text.stroke-97"),sQuery(id+"F13.wireOp",EDGE,"E13.sketch_text.stroke-98"),sQuery(id+"F13.wireOp",EDGE,"E13.sketch_text.stroke-99"),sQuery(id+"F13.wireOp",EDGE,"E13.sketch_text.stroke-100"),sQuery(id+"F13.wireOp",EDGE,"E13.sketch_text.stroke-101"),sQuery(id+"F13.wireOp",EDGE,"E13.sketch_text.stroke-102"),sQuery(id+"F13.wireOp",EDGE,"E13.sketch_text.stroke-103"),sQuery(id+"F13.wireOp",EDGE,"E13.sketch_text.stroke-104"),sQuery(id+"F13.wireOp",EDGE,"E13.sketch_text.stroke-105"),sQuery(id+"F13.wireOp",EDGE,"E13.sketch_text.stroke-106"),sQuery(id+"F13.wireOp",EDGE,"E13.sketch_text.stroke-107"),sQuery(id+"F13.wireOp",EDGE,"E13.sketch_text.stroke-108"),sQuery(id+"F13.wireOp",EDGE,"E13.sketch_text.stroke-109"),sQuery(id+"F13.wireOp",EDGE,"E13.sketch_text.stroke-110"),sQuery(id+"F13.wireOp",EDGE,"E13.sketch_text.stroke-111"),sQuery(id+"F13.wireOp",EDGE,"E13.sketch_text.stroke-112"),sQuery(id+"F13.wireOp",EDGE,"E13.sketch_text.stroke-113"),sQuery(id+"F13.wireOp",EDGE,"E13.sketch_text.stroke-114"),sQuery(id+"F13.wireOp",EDGE,"E13.sketch_text.stroke-115"),sQuery(id+"F13.wireOp",EDGE,"E13.sketch_text.stroke-116"),sQuery(id+"F13.wireOp",EDGE,"E13.sketch_text.stroke-117"),sQuery(id+"F13.wireOp",EDGE,"E13.sketch_text.stroke-118"),sQuery(id+"F13.wireOp",EDGE,"E13.sketch_text.stroke-119"),sQuery(id+"F13.wireOp",EDGE,"E13.sketch_text.stroke-120"),sQuery(id+"F13.wireOp",EDGE,"E13.sketch_text.stroke-121"),sQuery(id+"F13.wireOp",EDGE,"E13.sketch_text.stroke-122")])]});
            var Q6;
            Q6=makeQuery(id+"F14.opExtrude","SWEPT_BODY",BODY,{"disambiguationData":[OSD([sQuery(id+"F13.wireOp",EDGE,"E13.sketch_text.stroke-123"),sQuery(id+"F13.wireOp",EDGE,"E13.sketch_text.stroke-124"),sQuery(id+"F13.wireOp",EDGE,"E13.sketch_text.stroke-125"),sQuery(id+"F13.wireOp",EDGE,"E13.sketch_text.stroke-126"),sQuery(id+"F13.wireOp",EDGE,"E13.sketch_text.stroke-127"),sQuery(id+"F13.wireOp",EDGE,"E13.sketch_text.stroke-128"),sQuery(id+"F13.wireOp",EDGE,"E13.sketch_text.stroke-129"),sQuery(id+"F13.wireOp",EDGE,"E13.sketch_text.stroke-130"),sQuery(id+"F13.wireOp",EDGE,"E13.sketch_text.stroke-131"),sQuery(id+"F13.wireOp",EDGE,"E13.sketch_text.stroke-132"),sQuery(id+"F13.wireOp",EDGE,"E13.sketch_text.stroke-133"),sQuery(id+"F13.wireOp",EDGE,"E13.sketch_text.stroke-134"),sQuery(id+"F13.wireOp",EDGE,"E13.sketch_text.stroke-135")])]});
            var Q7;
            Q7=makeQuery(id+"F14.opExtrude","SWEPT_BODY",BODY,{"disambiguationData":[OSD([sQuery(id+"F13.wireOp",EDGE,"E13.sketch_text.stroke-136"),sQuery(id+"F13.wireOp",EDGE,"E13.sketch_text.stroke-137"),sQuery(id+"F13.wireOp",EDGE,"E13.sketch_text.stroke-138"),sQuery(id+"F13.wireOp",EDGE,"E13.sketch_text.stroke-139"),sQuery(id+"F13.wireOp",EDGE,"E13.sketch_text.stroke-140"),sQuery(id+"F13.wireOp",EDGE,"E13.sketch_text.stroke-141"),sQuery(id+"F13.wireOp",EDGE,"E13.sketch_text.stroke-142"),sQuery(id+"F13.wireOp",EDGE,"E13.sketch_text.stroke-143"),sQuery(id+"F13.wireOp",EDGE,"E13.sketch_text.stroke-144"),sQuery(id+"F13.wireOp",EDGE,"E13.sketch_text.stroke-145"),sQuery(id+"F13.wireOp",EDGE,"E13.sketch_text.stroke-146"),sQuery(id+"F13.wireOp",EDGE,"E13.sketch_text.stroke-147"),sQuery(id+"F13.wireOp",EDGE,"E13.sketch_text.stroke-148"),sQuery(id+"F13.wireOp",EDGE,"E13.sketch_text.stroke-149"),sQuery(id+"F13.wireOp",EDGE,"E13.sketch_text.stroke-150"),sQuery(id+"F13.wireOp",EDGE,"E13.sketch_text.stroke-151"),sQuery(id+"F13.wireOp",EDGE,"E13.sketch_text.stroke-152"),sQuery(id+"F13.wireOp",EDGE,"E13.sketch_text.stroke-153"),sQuery(id+"F13.wireOp",EDGE,"E13.sketch_text.stroke-154")])]});
            var Q8;
            Q8=makeQuery(id+"F14.opExtrude","SWEPT_BODY",BODY,{"disambiguationData":[OSD([sQuery(id+"F13.wireOp",EDGE,"E13.sketch_text.stroke-155"),sQuery(id+"F13.wireOp",EDGE,"E13.sketch_text.stroke-156"),sQuery(id+"F13.wireOp",EDGE,"E13.sketch_text.stroke-157"),sQuery(id+"F13.wireOp",EDGE,"E13.sketch_text.stroke-158"),sQuery(id+"F13.wireOp",EDGE,"E13.sketch_text.stroke-159"),sQuery(id+"F13.wireOp",EDGE,"E13.sketch_text.stroke-160"),sQuery(id+"F13.wireOp",EDGE,"E13.sketch_text.stroke-161"),sQuery(id+"F13.wireOp",EDGE,"E13.sketch_text.stroke-162"),sQuery(id+"F13.wireOp",EDGE,"E13.sketch_text.stroke-163"),sQuery(id+"F13.wireOp",EDGE,"E13.sketch_text.stroke-164"),sQuery(id+"F13.wireOp",EDGE,"E13.sketch_text.stroke-165"),sQuery(id+"F13.wireOp",EDGE,"E13.sketch_text.stroke-166"),sQuery(id+"F13.wireOp",EDGE,"E13.sketch_text.stroke-167"),sQuery(id+"F13.wireOp",EDGE,"E13.sketch_text.stroke-168"),sQuery(id+"F13.wireOp",EDGE,"E13.sketch_text.stroke-169"),sQuery(id+"F13.wireOp",EDGE,"E13.sketch_text.stroke-170"),sQuery(id+"F13.wireOp",EDGE,"E13.sketch_text.stroke-171"),sQuery(id+"F13.wireOp",EDGE,"E13.sketch_text.stroke-172"),sQuery(id+"F13.wireOp",EDGE,"E13.sketch_text.stroke-173"),sQuery(id+"F13.wireOp",EDGE,"E13.sketch_text.stroke-174"),sQuery(id+"F13.wireOp",EDGE,"E13.sketch_text.stroke-175"),sQuery(id+"F13.wireOp",EDGE,"E13.sketch_text.stroke-176"),sQuery(id+"F13.wireOp",EDGE,"E13.sketch_text.stroke-177"),sQuery(id+"F13.wireOp",EDGE,"E13.sketch_text.stroke-178"),sQuery(id+"F13.wireOp",EDGE,"E13.sketch_text.stroke-179")])]});
            var Q9;
            Q9=makeQuery(id+"F4.opExtrude","SWEPT_BODY",BODY,{"disambiguationData":[OSD([sQuery(id+"F3.wireOp",EDGE,"E9"),sQuery(id+"F3.wireOp",EDGE,"E10"),sQuery(id+"F3.wireOp",EDGE,"E11"),sQuery(id+"F3.wireOp",EDGE,"E12")])]});
            booleanBodies(context, id + "F18", {"operationType" : BooleanOperationType.SUBTRACTION, "tools" : qUnion([Q0, Q1, Q2, Q3, Q4, Q5, Q6, Q7, Q8]), "targets" : qUnion([Q9])});
        }
        {
            var Q0;
            Q0=qCreatedBy(id+"F10.planeOp",FACE);
            var sketch = newSketch(context, id + "F19", { "sketchPlane" : qUnion([Q0])});
            skCircle(sketch, "E15", {"center": v(0, 21.08) * mm, "radius": 2 * mm});
            skSolve(sketch);
        }
        {
            var Q0;
            Q0=makeQuery(id+"F19.imprint","IMPRINT",FACE,{"disambiguationData":[TD([[makeQuery(id+"F19.imprint","IMPRINT",EDGE,{"derivedFrom":sQuery(id+"F19.wireOp",EDGE,"E15")}),1.0]])]});
            extrude(context, id + "F20", {"entities" : qUnion([Q0]), "depth" : 25 * mm, "offsetDistance" : 25 * mm});
        }
        {
            var Q0;
            Q0=makeQuery(id+"F20.opExtrude","CAP_EDGE",EDGE,{"disambiguationData":[OSD([sQuery(id+"F19.wireOp",EDGE,"E15")])],"isStart":true});
            fillet(context, id + "F21", {"entities" : qUnion([Q0]), "radius" : 2 * mm, "tangentPropagation" : true, "allowEdgeOverflow" : false});
        }
        {
            var Q0;
            Q0=makeQuery(id+"F20.opExtrude","SWEPT_BODY",BODY,{"disambiguationData":[OSD([sQuery(id+"F19.wireOp",EDGE,"E15")])]});
            transform(context, id + "F22", {"entities" : qUnion([Q0]), "transformType" : TransformType.TRANSLATION_3D, "dx" : 16.4 * mm, "dy" : -4.8 * mm, "dz" : -10.6 * mm, "makeCopy" : true});
        }
        {
            var Q0;
            Q0=makeQuery(id+"F20.opExtrude","SWEPT_BODY",BODY,{"disambiguationData":[OSD([sQuery(id+"F19.wireOp",EDGE,"E15")])]});
            transform(context, id + "F23", {"entities" : qUnion([Q0]), "transformType" : TransformType.TRANSLATION_3D, "dx" : 8.3 * mm, "dy" : -2.5 * mm, "dz" : 0 * mm, "makeCopy" : false});
        }
        {
            var Q0;
            Q0=makeQuery(id+"F20.opExtrude","SWEPT_BODY",BODY,{"disambiguationData":[OSD([sQuery(id+"F19.wireOp",EDGE,"E15")])]});
            var Q1;
            Q1=makeQuery(id+"F22.opPattern","COPY",BODY,{"derivedFrom":makeQuery(id+"F20.opExtrude","SWEPT_BODY",BODY,{"disambiguationData":[OSD([sQuery(id+"F19.wireOp",EDGE,"E15")])]}),"instanceName":"1"});
            var Q2;
            Q2=qCreatedBy(makeId("Front.planeOp"),FACE);
            mirror(context, id + "F24", {"entities" : qUnion([Q0, Q1]), "mirrorPlane" : qUnion([Q2])});
        }
        {
            var Q0;
            Q0=makeQuery(id+"F20.opExtrude","SWEPT_BODY",BODY,{"disambiguationData":[OSD([sQuery(id+"F19.wireOp",EDGE,"E15")])]});
            var Q1;
            Q1=makeQuery(id+"F24.opPattern","COPY",BODY,{"derivedFrom":makeQuery(id+"F20.opExtrude","SWEPT_BODY",BODY,{"disambiguationData":[OSD([sQuery(id+"F19.wireOp",EDGE,"E15")])]}),"instanceName":"1"});
            var Q2;
            Q2=makeQuery(id+"F22.opPattern","COPY",BODY,{"derivedFrom":makeQuery(id+"F20.opExtrude","SWEPT_BODY",BODY,{"disambiguationData":[OSD([sQuery(id+"F19.wireOp",EDGE,"E15")])]}),"instanceName":"1"});
            var Q3;
            Q3=makeQuery(id+"F24.opPattern","COPY",BODY,{"derivedFrom":makeQuery(id+"F22.opPattern","COPY",BODY,{"derivedFrom":makeQuery(id+"F20.opExtrude","SWEPT_BODY",BODY,{"disambiguationData":[OSD([sQuery(id+"F19.wireOp",EDGE,"E15")])]}),"instanceName":"1"}),"instanceName":"1"});
            var Q4;
            Q4=makeQuery(id+"F4.opExtrude","SWEPT_BODY",BODY,{"disambiguationData":[OSD([sQuery(id+"F3.wireOp",EDGE,"E9"),sQuery(id+"F3.wireOp",EDGE,"E10"),sQuery(id+"F3.wireOp",EDGE,"E11"),sQuery(id+"F3.wireOp",EDGE,"E12")])]});
            booleanBodies(context, id + "F25", {"operationType" : BooleanOperationType.SUBTRACTION, "tools" : qUnion([Q0, Q1, Q2, Q3]), "targets" : qUnion([Q4])});
        }
    });
